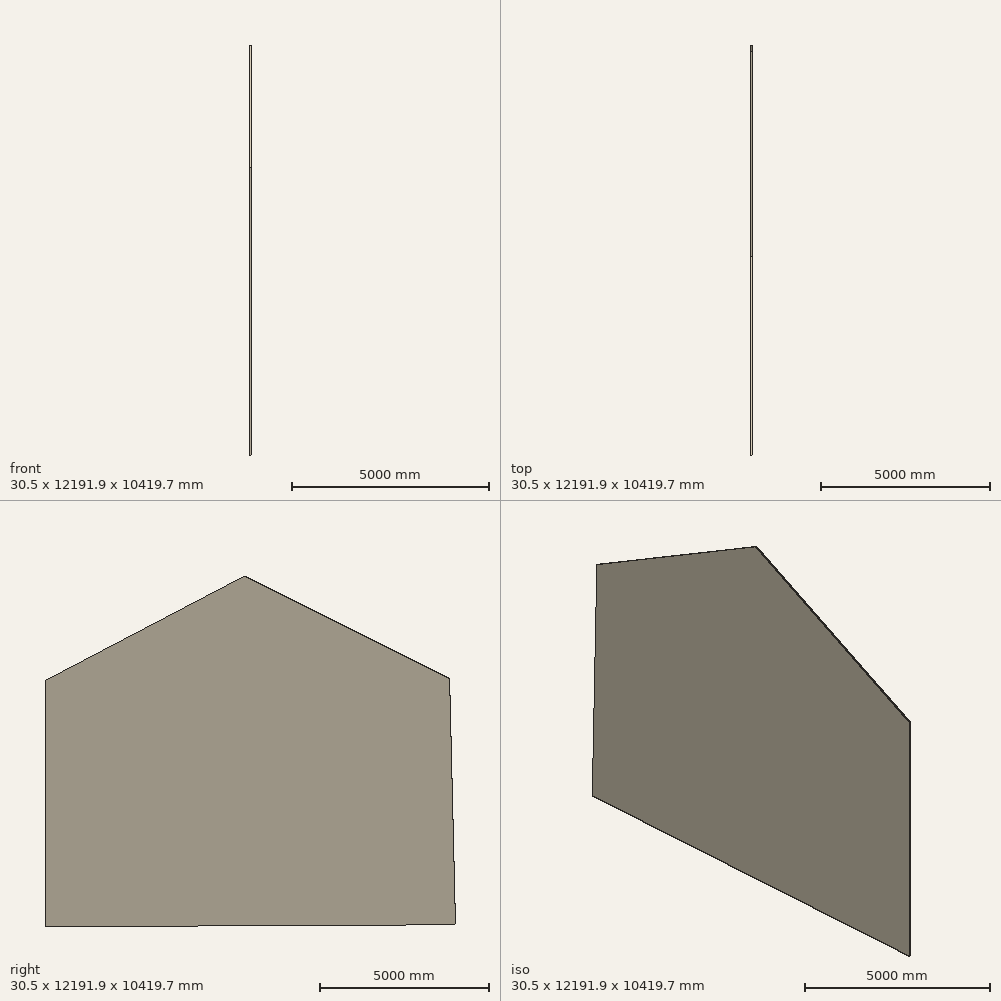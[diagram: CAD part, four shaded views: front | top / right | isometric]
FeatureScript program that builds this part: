
annotation { "Feature Type Name" : "Feature", "Feature Type Description" : "" }
export const myFeature = defineFeature(function(context is Context, id is Id, definition is map)
    precondition{}
    {
        {
            var Q0;
            Q0=qCreatedBy(makeId("Right.planeOp"),FACE);
            var sketch = newSketch(context, id + "F0", { "sketchPlane" : qUnion([Q0])});
            skLineSegment(sketch, "E0", {"start": v(5920.04, 56.5) * mm, "end": v(-175.96, 56.5) * mm});
            skLineSegment(sketch, "E1", {"start": v(5920.04, 56.5) * mm, "end": v(12016.04, 56.5) * mm});
            skLineSegment(sketch, "E2", {"start": v(5920.04, 56.5) * mm, "end": v(5920.04, 3104.5) * mm});
            skLineSegment(sketch, "E3", {"start": v(5920.04, 3104.5) * mm, "end": v(0, 0) * mm});
            skLineSegment(sketch, "E4", {"start": v(5920.04, 3104.5) * mm, "end": v(12016.04, 56.5) * mm});
            skLineSegment(sketch, "E5", {"start": v(0, 0) * mm, "end": v(0, -7315.2) * mm});
            skLineSegment(sketch, "E6", {"start": v(12016.04, 56.5) * mm, "end": v(12191.86, -7256.6) * mm});
            skLineSegment(sketch, "E7", {"start": v(12191.86, -7256.6) * mm, "end": v(0, -7315.2) * mm});
            skLineSegment(sketch, "E8", {"start": v(6095.93, -7285.9) * mm, "end": v(6087.14, -5457.12) * mm});
            skLineSegment(sketch, "E9", {"start": v(6087.14, -5457.12) * mm, "end": v(4868.3, -5486.42) * mm});
            skLineSegment(sketch, "E10", {"start": v(4401.3, -5486.42) * mm, "end": v(4410.08, -7315.2) * mm});
            skLineSegment(sketch, "E11", {"start": v(4668.68, -1319.06) * mm, "end": v(2839.88, -1319.06) * mm});
            skLineSegment(sketch, "E12", {"start": v(2839.88, -1319.06) * mm, "end": v(2839.88, -2538.26) * mm});
            skLineSegment(sketch, "E13", {"start": v(2839.88, -2538.26) * mm, "end": v(4668.68, -2538.26) * mm});
            skLineSegment(sketch, "E14", {"start": v(4668.68, -2538.26) * mm, "end": v(4668.68, -1319.06) * mm});
            skLineSegment(sketch, "E15", {"start": v(9646.68, -1446.76) * mm, "end": v(7208.28, -1446.76) * mm});
            skLineSegment(sketch, "E16", {"start": v(7208.28, -1446.76) * mm, "end": v(7208.28, -2361.16) * mm});
            skLineSegment(sketch, "E17", {"start": v(7387.05, -2379.92) * mm, "end": v(9825.38, -2361.16) * mm});
            skLineSegment(sketch, "E18", {"start": v(9646.68, -1446.76) * mm, "end": v(9884.41, -1446.76) * mm});
            skLineSegment(sketch, "E19", {"start": v(9884.41, -1446.76) * mm, "end": v(9884.41, -2361.16) * mm});
            skSolve(sketch);
        }
        {
            var Q0;
            Q0=makeQuery(id+"F0.imprint","IMPRINT",FACE,{"disambiguationData":[TD([[makeQuery(id+"F0.imprint","IMPRINT",EDGE,{"derivedFrom":sQuery(id+"F0.wireOp",EDGE,"E11")}),1.0]])]});
            var Q1;
            {var subQ0=sQuery(id+"F0.wireOp",EDGE,"E2");Q1=makeQuery(id+"F0.imprint","IMPRINT",FACE,{"disambiguationData":[TD([[makeQuery(id+"F0.imprint","IMPRINT",EDGE,{"derivedFrom":subQ0}),1.0]])]});}
            var Q2;
            Q2=makeQuery(id+"F0.imprint","IMPRINT",FACE,{"disambiguationData":[TD([[makeQuery(id+"F0.imprint","IMPRINT",EDGE,{"derivedFrom":sQuery(id+"F0.wireOp",EDGE,"E1")}),1.0]])]});
            var Q3;
            {var subQ4=sQuery(id+"F0.wireOp",EDGE,"E1");Q3=makeQuery(id+"F0.imprint","IMPRINT",FACE,{"disambiguationData":[TD([[makeQuery(id+"F0.imprint","IMPRINT",EDGE,{"derivedFrom":subQ4}),-1.0]])]});}
            extrude(context, id + "F1", {"entities" : qUnion([Q0, Q1, Q2, Q3]), "depth" : 30.48 * mm, "offsetDistance" : 30.48 * mm});
        }
    });
